# Revit family: Masterwatt Calida Compact
name_source: partatom
category: Mechanical Equipment
revit_build: Autodesk Revit 2018 (Build: 20190510_1515(x64)
units: mm (PartAtom-declared; Revit-internal decimal feet)

## family parameters
Always vertical = Yes
Classification = None
Cut with Voids When Loaded = No
OmniClass Number = 23.75.10.11.14
OmniClass Title = Hot Water Heat Generators
Part Type = Normal
Room Calculation Point = No
Round Connector Dimension = Use Diameter
Shared = No
Work Plane-Based = No

## types (2) — shared parameters
Diepte = 191 mm  [stored 0.62664 ft]
Diepte aansluiting = 117 mm  [stored 0.383858 ft]
Hoogte = 716 mm  [stored 2.34908 ft]
Hoogte bedieningspaneel = 310 mm  [stored 1.01706 ft]
Materiaal_01 = Coating wit
Model = EKCO.L3
URL = https://masterwatt.nl

## per-type parameters (varying)
| type | Art. No. | Voltage | Watt |
| EKCO.L3_4/6/8 kW | 300 100 008 | 230 V | 8000 VA |
| EKCO.L3_12/16/20/24 kW | 300 100 024 | 400 V | 24000 VA |

note: [stored X ft] marks values corroborated as IEEE doubles in the binary element streams (Revit-internal decimal feet)

## geometry (parser evidence)
native form markers: Sweep x6
no freeform markers — native parametric forms only
